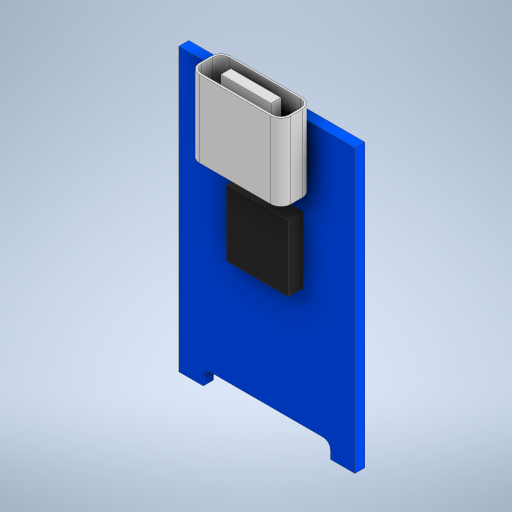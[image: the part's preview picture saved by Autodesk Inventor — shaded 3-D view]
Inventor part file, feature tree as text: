
AUTODESK INVENTOR PART (.ipt)
format: ipt  version: 2023.1 (Build 271208000, 208)  size: 345,600 bytes
history: native  units: mm
features: extrude x4, sketch x4, other x1, fillet x1, projected_geometry x1
ambient origin geometry x8: Origin, YZ Plane, XZ Plane, XY Plane, X Axis, Y Axis, Z Axis, Center Point
bodies: Body1 (feature_tree)
feature tree (11):
  other  "솔리드1"
  extrude  "돌출1"  Depth=17.5mm
  extrude  "돌출2"  Depth=28.0mm
  fillet  "모깎기1"  Radius=2.44mm
  extrude  "돌출3"  Depth=1.54mm
  extrude  "돌출4"  Depth=1.0mm TaperAngle=0.0deg
  sketch  "스케치1"
  sketch  "스케치2"
  sketch  "스케치3"
  projected_geometry  "투영된 루프1"
  sketch  "스케치4"
